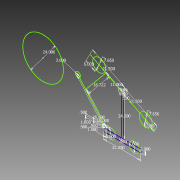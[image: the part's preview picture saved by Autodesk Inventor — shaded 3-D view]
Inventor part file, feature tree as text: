
AUTODESK INVENTOR PART (.ipt)
format: ipt  version: 2014 SP1 (Build 180222100, 222)  size: 96,256 bytes
history: native  units: in
note: dims shown in document units (in); Inventor stores cm internally (conversion verified against a paired STEP export)
features: sketch x1
ambient origin geometry x8: Origin, YZ Plane, XZ Plane, XY Plane, X Axis, Y Axis, Z Axis, Center Point
feature tree (1):
  sketch  "Sketch1"  dims[d0=22.0in d1=2.0in d2=6.0in d3=6.0in d4=1.5in d5=1.0in d6=0.5in d9=0.5in d10=0.5in d11=3.0in d50=1.0in d51=24.0in d52=0.5in d53=0.5in d54=0.5in d55=0.5in d56=21.5in d57=21.5in d58=7.65in d59=7.65in d60=6.0in d62=6.0in d65=18.0in d70=11.0in d71=25.0in d75=18.722in d76=24.0in]
